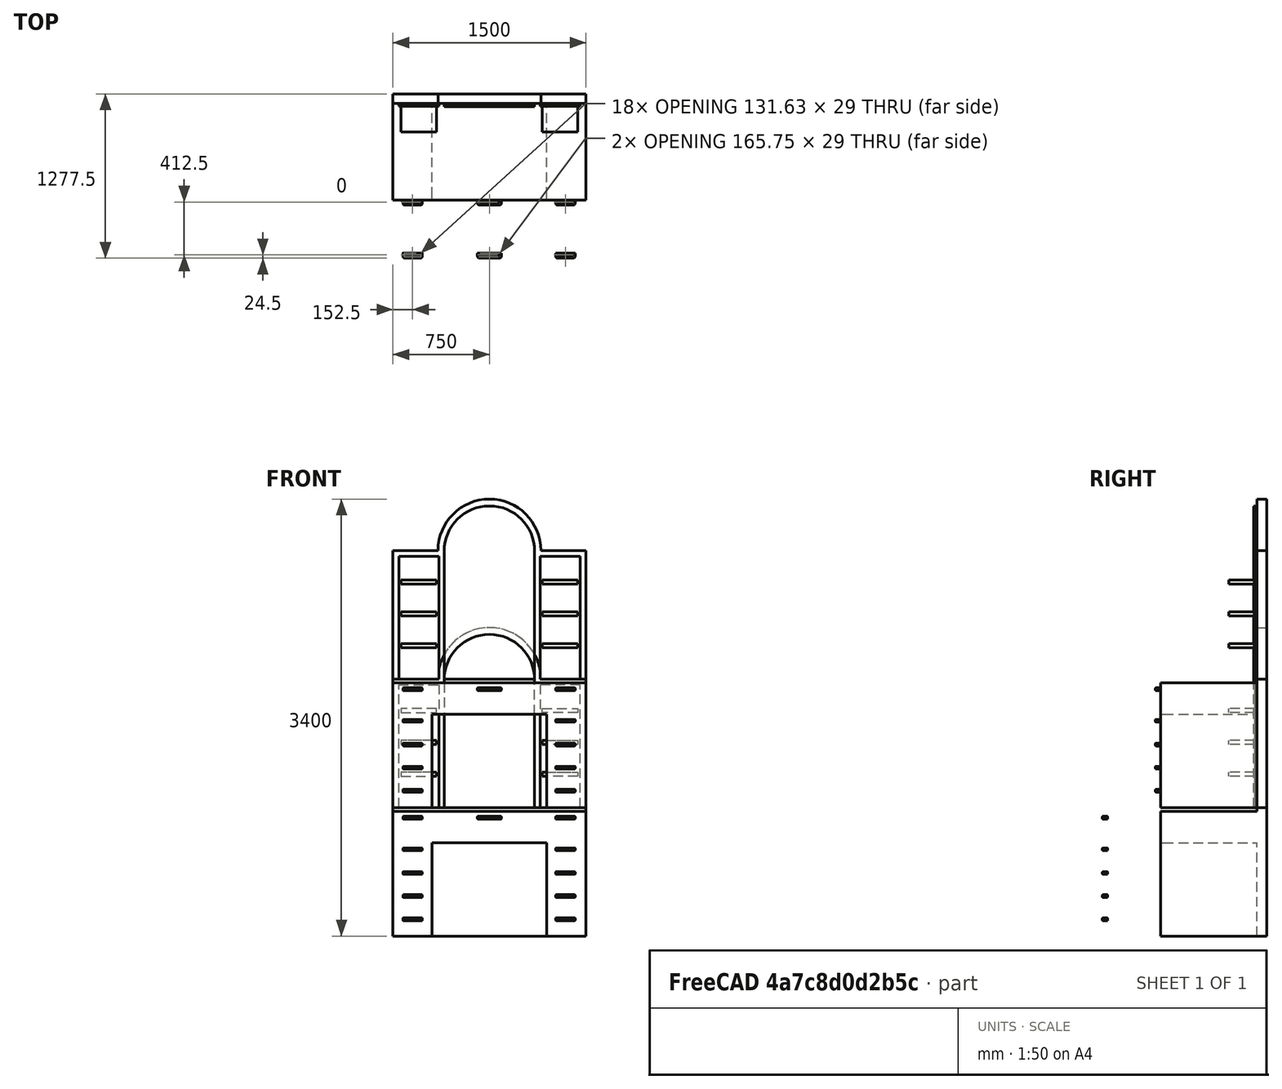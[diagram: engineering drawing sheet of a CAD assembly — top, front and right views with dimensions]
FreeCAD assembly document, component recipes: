
FREECAD ASSEMBLY — COMPONENT RECIPES ("DressingTable")

This assembly document has 3 components, labeled P0..P2 below (a component is one placed body or linked part). 3 of them carry a construction recipe — the FreeCAD feature program that regenerates the part from scratch, quoted from this document or its linked companion documents; the rest are supplied as boundary geometry only. No exploded tour is included for this assembly.
COMPONENT P0 — recipe-attached ("Body013", modeled in this document).
Construction recipe (the document's own serialized feature program — sketch geometry with constraints, then the solid features built on it; lengths are millimeters unless a unit is written):

FEATURE [PartDesign::ShapeBinder] CopyPad005
  Placement = pos=(0,-20,9e-15) rot=(0,0,1;0rad)
  TraceSupport = false
FEATURE [PartDesign::Plane] DatumPlane011
  AttachmentSupport = -> [CopyPad005]
  Length = 899.662
  MapMode = 5
  Placement = pos=(0,-95,2.55e-14) rot=(1,0,0;1.5708rad)
  ResizeMode = 0
  Width = 1568.05
FEATURE [Sketcher::SketchObject] Sketch030
  ArcFitTolerance = 1e-06
  AttachmentSupport = -> [CopyPad005]
  ExternalGeometry = -> [CopyPad005]
  FullyConstrained = false
  MakeInternals = false
  MapMode = 5
  Placement = pos=(0,-95,2.55e-14) rot=(1,0,0;1.5708rad)
  sketch-geometry (4):
    g0: LineSegment StartX=-351.618 StartY=995.137 StartZ=0 EndX=-351.618 EndY=0 EndZ=0
    g1: LineSegment StartX=-351.618 StartY=0 StartZ=0 EndX=351.618 EndY=0 EndZ=0
    g2: LineSegment StartX=351.618 StartY=0 StartZ=0 EndX=351.618 EndY=995.137 EndZ=0
    g3: ArcOfCircle CenterX=1.05374e-11 CenterY=995.137 CenterZ=0 NormalX=0 NormalY=0 NormalZ=1 AngleXU=0 Radius=351.618 StartAngle=8.98854e-10 EndAngle=3.14159
  constraints (10):
    c: Coincident(g0,g1)
    c: Coincident(g1,g2)
    c: Vertical(g0)
    c: Vertical(g2)
    c: Horizontal(g1)
    c: Coincident(g0,g-4)
    c: Coincident(g1,g-3)
    c: Coincident(g3,g0)
    c: Coincident(g3,g2)
    c: Tangent(g3,g-5)
FEATURE [PartDesign::Pad] Pad017
  Direction = (0,-1,2e-16)
  Length = 5
  Length2 = 10
  Placement = pos=(0,-20,9e-15) rot=(0,0,1;0rad)
  Profile = -> Sketch030
  ReferenceAxis = -> Sketch030 [N_Axis]
  Refine = true
  Suppressed = false
  Type = 0
FEATURE [PartDesign::Body] Body012
  AllowCompound = false
  Group = -> [DatumPlane011,CopyPad005,Sketch030,Pad017]
  Origin = -> Origin020
  Placement = pos=(0,412.5,0) rot=(0,0,1;0rad)
  Tip = -> Pad017
COMPONENT P1 — recipe-attached ("dressing_table002", modeled in this document).
Construction recipe (the document's own serialized feature program — sketch geometry with constraints, then the solid features built on it; lengths are millimeters unless a unit is written):

FEATURE [Sketcher::SketchObject] Sketch
  ArcFitTolerance = 1e-06
  AttachmentSupport = -> [XZ_Plane]
  FullyConstrained = true
  MakeInternals = false
  MapMode = 5
  Placement = pos=(0,0,0) rot=(1,0,0;1.5708rad)
  sketch-geometry (7):
    g0: LineSegment StartX=-750 StartY=-1000 StartZ=0 EndX=750 EndY=-1000 EndZ=0
    g1: LineSegment StartX=750 StartY=-1000 StartZ=0 EndX=750 EndY=1000 EndZ=0
    g2: LineSegment StartX=750 StartY=1000 StartZ=0 EndX=400 EndY=1000 EndZ=0
    g3: LineSegment StartX=-750 StartY=1000 StartZ=0 EndX=-750 EndY=-1000 EndZ=0
    g4: GeomPoint [constr] X=0 Y=0 Z=0
    g5: ArcOfCircle CenterX=1.35e-14 CenterY=1000 CenterZ=0 NormalX=0 NormalY=0 NormalZ=1 AngleXU=0 Radius=400 StartAngle=0 EndAngle=3.14159
    g6: LineSegment StartX=-400 StartY=1000 StartZ=0 EndX=-750 EndY=1000 EndZ=0
  constraints (18):
    c: Coincident(g0,g1)
    c: Coincident(g1,g2)
    c: Coincident(g6,g3)
    c: Coincident(g3,g0)
    c: Horizontal(g0)
    c: Horizontal(g2)
    c: Vertical(g1)
    c: Vertical(g3)
    c: Symmetric(g2,g0,g4)
    c: Coincident(g4,g-1)
    c: DistanceY(g1,g1) = 2000
    c: DistanceX(g6,g2) = 1500
    c: Symmetric(g1,g6,g5)
    c: Diameter(g5) = 800
    c: Coincident(g5,g6)
    c: Coincident(g5,g2)
    c: Horizontal(g6)
    c: Horizontal(g5,g2)
FEATURE [PartDesign::Pad] Pad
  Direction = (0,-1,2e-16)
  Length = 75
  Length2 = 10
  Placement = pos=(0,0,0) rot=(1,0,0;1.5708rad)
  Profile = -> Sketch
  ReferenceAxis = -> Sketch [N_Axis]
  Refine = true
  Suppressed = false
  Type = 0
FEATURE [Sketcher::SketchObject] Sketch001
  ArcFitTolerance = 1e-06
  AttachmentSupport = -> [Pad]
  FullyConstrained = false
  MakeInternals = false
  MapMode = 5
  Placement = pos=(0,-75,0) rot=(1,0,0;1.5708rad)
  sketch-geometry (14):
    g0: LineSegment [constr] StartX=0 StartY=0 StartZ=0 EndX=936.468 EndY=0 EndZ=0
    g1: LineSegment [constr] StartX=0 StartY=0 StartZ=0 EndX=-879.559 EndY=0 EndZ=0
    g2: ArcOfCircle CenterX=0 CenterY=995.137 CenterZ=0 NormalX=0 NormalY=0 NormalZ=1 AngleXU=0 Radius=351.618 StartAngle=0 EndAngle=3.14159
    g3: LineSegment StartX=-351.618 StartY=995.137 StartZ=0 EndX=-351.618 EndY=0 EndZ=0
    g4: LineSegment StartX=351.618 StartY=995.137 StartZ=0 EndX=351.618 EndY=0 EndZ=0
    g5: LineSegment StartX=-351.618 StartY=0 StartZ=0 EndX=351.618 EndY=0 EndZ=0
    g6: LineSegment StartX=393.332 StartY=955.725 StartZ=0 EndX=393.332 EndY=0 EndZ=0
    g7: LineSegment StartX=393.332 StartY=0 StartZ=0 EndX=704.851 EndY=0 EndZ=0
    g8: LineSegment StartX=704.851 StartY=0 StartZ=0 EndX=704.851 EndY=955.725 EndZ=0
    g9: LineSegment StartX=704.851 StartY=955.725 StartZ=0 EndX=393.332 EndY=955.725 EndZ=0
    g10: LineSegment StartX=-393.332 StartY=955.725 StartZ=0 EndX=-393.332 EndY=0 EndZ=0
    g11: LineSegment StartX=-393.332 StartY=0 StartZ=0 EndX=-704.851 EndY=0 EndZ=0
    g12: LineSegment StartX=-704.851 StartY=0 StartZ=0 EndX=-704.851 EndY=955.725 EndZ=0
    g13: LineSegment StartX=-704.851 StartY=955.725 StartZ=0 EndX=-393.332 EndY=955.725 EndZ=0
  constraints (30):
    c: Coincident(g0,g-1)
    c: Horizontal(g0)
    c: Coincident(g1,g0)
    c: PointOnObject(g1,g-1)
    c: PointOnObject(g2,g-2)
    c: PointOnObject(g3,g1)
    c: Vertical(g3)
    c: PointOnObject(g4,g0)
    c: Vertical(g4)
    c: Tangent(g4,g2) = 1.5708
    c: Tangent(g3,g2) = -1.5708
    c: Coincident(g5,g3)
    c: Coincident(g5,g4)
    c: Coincident(g6,g7)
    c: Coincident(g7,g8)
    c: Coincident(g8,g9)
    c: Coincident(g9,g6)
    c: Vertical(g6)
    c: Vertical(g8)
    c: Horizontal(g7)
    c: Horizontal(g9)
    c: PointOnObject(g7,g0)
    c: Coincident(g10,g11)
    c: Coincident(g11,g12)
    c: Coincident(g12,g13)
    c: Coincident(g13,g10)
    c: Vertical(g10)
    c: Vertical(g12)
    c: Horizontal(g11)
    c: Horizontal(g13)
FEATURE [PartDesign::Pad] Pad001
  BaseFeature = -> Pad
  Direction = (0,-1,2e-16)
  Length = 20
  Length2 = 10
  Placement = pos=(0,0,0) rot=(1,0,0;1.5708rad)
  Profile = -> Sketch001
  ReferenceAxis = -> Sketch001 [N_Axis]
  Refine = true
  Suppressed = false
  Type = 0
FEATURE [Sketcher::SketchObject] Sketch002
  ArcFitTolerance = 1e-06
  AttachmentSupport = -> [Pad001]
  ExternalGeometry = -> [Pad001]
  FullyConstrained = false
  MakeInternals = false
  MapMode = 5
  Placement = pos=(0,-95,2.09e-14) rot=(1,0,0;1.5708rad)
  sketch-geometry (27):
    g0: LineSegment StartX=-686.592 StartY=770.22 StartZ=0 EndX=-686.592 EndY=738.354 EndZ=0
    g1: LineSegment StartX=-686.592 StartY=738.354 StartZ=0 EndX=-411.592 EndY=738.354 EndZ=0
    g2: LineSegment StartX=-411.592 StartY=738.354 StartZ=0 EndX=-411.592 EndY=770.22 EndZ=0
    g3: LineSegment StartX=-411.592 StartY=770.22 StartZ=0 EndX=-686.592 EndY=770.22 EndZ=0
    g4: LineSegment StartX=-686.592 StartY=523.301 StartZ=0 EndX=-686.592 EndY=491.435 EndZ=0
    g5: LineSegment StartX=-686.592 StartY=491.435 StartZ=0 EndX=-411.592 EndY=491.435 EndZ=0
    g6: LineSegment StartX=-411.592 StartY=491.435 StartZ=0 EndX=-411.592 EndY=523.301 EndZ=0
    g7: LineSegment StartX=-411.592 StartY=523.301 StartZ=0 EndX=-686.592 EndY=523.301 EndZ=0
    g8: LineSegment StartX=-686.592 StartY=276.382 StartZ=0 EndX=-686.592 EndY=244.516 EndZ=0
    g9: LineSegment StartX=-686.592 StartY=244.516 StartZ=0 EndX=-411.592 EndY=244.516 EndZ=0
    g10: LineSegment StartX=-411.592 StartY=244.516 StartZ=0 EndX=-411.592 EndY=276.382 EndZ=0
    g11: LineSegment StartX=-411.592 StartY=276.382 StartZ=0 EndX=-686.592 EndY=276.382 EndZ=0
    g12: LineSegment [constr] StartX=-686.592 StartY=738.354 StartZ=0 EndX=-686.592 EndY=523.301 EndZ=0
    g13: LineSegment [constr] StartX=-686.592 StartY=491.435 StartZ=0 EndX=-686.592 EndY=276.382 EndZ=0
    g14: LineSegment [constr] StartX=-549.092 StartY=477.863 StartZ=0 EndX=-549.092 EndY=955.725 EndZ=0
    g15: LineSegment StartX=686.592 StartY=738.354 StartZ=0 EndX=411.592 EndY=738.354 EndZ=0
    g16: LineSegment StartX=411.592 StartY=770.22 StartZ=0 EndX=686.592 EndY=770.22 EndZ=0
    g17: LineSegment StartX=411.592 StartY=738.354 StartZ=0 EndX=411.592 EndY=770.22 EndZ=0
    g18: LineSegment StartX=686.592 StartY=770.22 StartZ=0 EndX=686.592 EndY=738.354 EndZ=0
    g19: LineSegment StartX=411.592 StartY=523.301 StartZ=0 EndX=686.592 EndY=523.301 EndZ=0
    g20: LineSegment StartX=411.592 StartY=491.435 StartZ=0 EndX=411.592 EndY=523.301 EndZ=0
    g21: LineSegment StartX=686.592 StartY=491.435 StartZ=0 EndX=411.592 EndY=491.435 EndZ=0
    g22: LineSegment StartX=686.592 StartY=523.301 StartZ=0 EndX=686.592 EndY=491.435 EndZ=0
    g23: LineSegment StartX=411.592 StartY=244.516 StartZ=0 EndX=411.592 EndY=276.382 EndZ=0
    g24: LineSegment StartX=686.592 StartY=244.516 StartZ=0 EndX=411.592 EndY=244.516 EndZ=0
    g25: LineSegment StartX=411.592 StartY=276.382 StartZ=0 EndX=686.592 EndY=276.382 EndZ=0
    g26: LineSegment StartX=686.592 StartY=276.382 StartZ=0 EndX=686.592 EndY=244.516 EndZ=0
  constraints (66):
    c: Coincident(g0,g1)
    c: Coincident(g1,g2)
    c: Coincident(g2,g3)
    c: Coincident(g3,g0)
    c: Vertical(g0)
    c: Vertical(g2)
    c: Horizontal(g1)
    c: Horizontal(g3)
    c: Coincident(g4,g5)
    c: Coincident(g5,g6)
    c: Coincident(g6,g7)
    c: Coincident(g7,g4)
    c: Vertical(g4)
    c: Vertical(g6)
    c: Horizontal(g5)
    c: Horizontal(g7)
    c: Coincident(g8,g9)
    c: Coincident(g9,g10)
    c: Coincident(g10,g11)
    c: Coincident(g11,g8)
    c: Vertical(g8)
    c: Vertical(g10)
    c: Horizontal(g9)
    c: Horizontal(g11)
    c: Coincident(g12,g0)
    c: Coincident(g12,g4)
    c: Vertical(g12)
    c: Coincident(g13,g4)
    c: Coincident(g13,g8)
    c: Vertical(g13)
    c: Equal(g12,g13)
    c: Equal(g2,g6)
    c: Equal(g6,g10)
    c: Equal(g11,g7)
    c: Equal(g7,g3)
    c: DistanceX(g3,g3) = 275
    c: Symmetric(g2,g0,g14)
    c: Symmetric(g-5,g-5,g14)
    c: Coincident(g18,g15)
    c: Coincident(g15,g17)
    c: Coincident(g17,g16)
    c: Coincident(g16,g18)
    c: Vertical(g18)
    c: Vertical(g17)
    c: Horizontal(g15)
    c: Horizontal(g16)
    c: Coincident(g22,g21)
    c: Coincident(g21,g20)
    c: Coincident(g20,g19)
    c: Coincident(g19,g22)
    c: Vertical(g22)
    c: Vertical(g20)
    c: Horizontal(g21)
    c: Horizontal(g19)
    c: Coincident(g26,g24)
    c: Coincident(g24,g23)
    c: Coincident(g23,g25)
    c: Coincident(g25,g26)
    c: Vertical(g26)
    c: Vertical(g23)
    c: Horizontal(g24)
    c: Horizontal(g25)
    c: Equal(g17,g20)
    c: Equal(g20,g23)
    c: Equal(g25,g19)
    c: Equal(g19,g16)
FEATURE [PartDesign::Pad] Pad002
  BaseFeature = -> Pad001
  Direction = (0,-1,2e-16)
  Length = 200
  Length2 = 10
  Placement = pos=(0,0,0) rot=(1,0,0;1.5708rad)
  Profile = -> Sketch002
  ReferenceAxis = -> Sketch002 [N_Axis]
  Refine = true
  Suppressed = false
  Type = 0
FEATURE [Sketcher::SketchObject] Sketch003
  ArcFitTolerance = 1e-06
  AttachmentSupport = -> [Pad002]
  ExternalGeometry = -> [Pad002]
  FullyConstrained = true
  MakeInternals = false
  MapMode = 5
  Placement = pos=(0,-75,0) rot=(1,0,0;1.5708rad)
  sketch-geometry (4):
    g0: LineSegment StartX=-750 StartY=-1000 StartZ=0 EndX=750 EndY=-1000 EndZ=0
    g1: LineSegment StartX=750 StartY=-1000 StartZ=0 EndX=750 EndY=-30 EndZ=0
    g2: LineSegment StartX=750 StartY=-30 StartZ=0 EndX=-750 EndY=-30 EndZ=0
    g3: LineSegment StartX=-750 StartY=-30 StartZ=0 EndX=-750 EndY=-1000 EndZ=0
  constraints (11):
    c: Coincident(g0,g1)
    c: Coincident(g1,g2)
    c: Coincident(g2,g3)
    c: Coincident(g3,g0)
    c: Horizontal(g0)
    c: Horizontal(g2)
    c: Vertical(g1)
    c: Vertical(g3)
    c: Coincident(g0,g-3)
    c: PointOnObject(g1,g-4)
    c: DistanceY(g1,g1) = 970
FEATURE [PartDesign::Pad] Pad003
  BaseFeature = -> Pad002
  Direction = (0,-1,2e-16)
  Length = 750
  Length2 = 10
  Placement = pos=(0,0,0) rot=(1,0,0;1.5708rad)
  Profile = -> Sketch003
  ReferenceAxis = -> Sketch003 [N_Axis]
  Suppressed = false
  Type = 0
FEATURE [Sketcher::SketchObject] Sketch004
  ArcFitTolerance = 1e-06
  AttachmentSupport = -> [Pad003]
  ExternalGeometry = -> [Pad003]
  FullyConstrained = true
  MakeInternals = false
  MapMode = 5
  Placement = pos=(0,-825,1.897e-13) rot=(1,0,0;1.5708rad)
  sketch-geometry (4):
    g0: LineSegment StartX=-445 StartY=-1000 StartZ=0 EndX=445 EndY=-1000 EndZ=0
    g1: LineSegment StartX=445 StartY=-1000 StartZ=0 EndX=445 EndY=-275 EndZ=0
    g2: LineSegment StartX=445 StartY=-275 StartZ=0 EndX=-445 EndY=-275 EndZ=0
    g3: LineSegment StartX=-445 StartY=-275 StartZ=0 EndX=-445 EndY=-1000 EndZ=0
  constraints (11):
    c: Coincident(g0,g1)
    c: Coincident(g1,g2)
    c: Coincident(g2,g3)
    c: Coincident(g3,g0)
    c: Horizontal(g0)
    c: Vertical(g1)
    c: Vertical(g3)
    c: PointOnObject(g0,g-3)
    c: DistanceX(g2,g2) = 890
    c: DistanceY(g1,g1) = 725
    c: Symmetric(g1,g2,g-2)
FEATURE [PartDesign::Pocket] Pocket
  BaseFeature = -> Pad003
  Direction = (0,1,-2e-16)
  Length = 750
  Length2 = 5
  Placement = pos=(0,0,0) rot=(1,0,0;1.5708rad)
  Profile = -> Sketch004
  ReferenceAxis = -> Sketch004 [N_Axis]
  Suppressed = false
  Type = 0
FEATURE [Sketcher::SketchObject] Sketch005
  ArcFitTolerance = 1e-06
  AttachmentSupport = -> [Pocket]
  ExternalGeometry = -> [Pocket]
  FullyConstrained = true
  MakeInternals = false
  MapMode = 5
  Placement = pos=(0,-825,1.897e-13) rot=(1,0,0;1.5708rad)
  sketch-geometry (24):
    g0: LineSegment StartX=-445 StartY=-275 StartZ=0 EndX=-445 EndY=-30 EndZ=0
    g1: LineSegment StartX=-445 StartY=-30 StartZ=0 EndX=-750 EndY=-30 EndZ=0
    g2: LineSegment StartX=-750 StartY=-30 StartZ=0 EndX=-750 EndY=-275 EndZ=0
    g3: LineSegment StartX=-750 StartY=-275 StartZ=0 EndX=-445 EndY=-275 EndZ=0
    g4: LineSegment StartX=-445 StartY=-460 StartZ=0 EndX=-750 EndY=-460 EndZ=0
    g5: LineSegment StartX=-750 StartY=-460 StartZ=0 EndX=-750 EndY=-640 EndZ=0
    g6: LineSegment StartX=-750 StartY=-640 StartZ=0 EndX=-445 EndY=-640 EndZ=0
    g7: LineSegment StartX=-445 StartY=-640 StartZ=0 EndX=-445 EndY=-460 EndZ=0
    g8: LineSegment StartX=-750 StartY=-820 StartZ=0 EndX=-445 EndY=-820 EndZ=0
    g9: LineSegment StartX=-750 StartY=-820 StartZ=0 EndX=-750 EndY=-1000 EndZ=0
    g10: LineSegment StartX=-750 StartY=-1000 StartZ=0 EndX=-445 EndY=-1000 EndZ=0
    g11: LineSegment StartX=-445 StartY=-1000 StartZ=0 EndX=-445 EndY=-820 EndZ=0
    g12: LineSegment StartX=750 StartY=-30 StartZ=0 EndX=750 EndY=-275 EndZ=0
    g13: LineSegment StartX=445 StartY=-30 StartZ=0 EndX=750 EndY=-30 EndZ=0
    g14: LineSegment StartX=750 StartY=-275 StartZ=0 EndX=445 EndY=-275 EndZ=0
    g15: LineSegment StartX=445 StartY=-460 StartZ=0 EndX=750 EndY=-460 EndZ=0
    g16: LineSegment StartX=750 StartY=-460 StartZ=0 EndX=750 EndY=-640 EndZ=0
    g17: LineSegment StartX=750 StartY=-640 StartZ=0 EndX=445 EndY=-640 EndZ=0
    g18: LineSegment StartX=445 StartY=-640 StartZ=0 EndX=445 EndY=-460 EndZ=0
    g19: LineSegment StartX=445 StartY=-1000 StartZ=0 EndX=445 EndY=-820 EndZ=0
    g20: LineSegment StartX=750 StartY=-1000 StartZ=0 EndX=445 EndY=-1000 EndZ=0
    g21: LineSegment StartX=750 StartY=-820 StartZ=0 EndX=750 EndY=-1000 EndZ=0
    g22: LineSegment StartX=750 StartY=-820 StartZ=0 EndX=445 EndY=-820 EndZ=0
    g23: LineSegment StartX=445 StartY=-30 StartZ=0 EndX=445 EndY=-275 EndZ=0
  constraints (67):
    c: Coincident(g0,g1)
    c: Vertical(g0)
    c: Horizontal(g1)
    c: Coincident(g0,g-6)
    c: Coincident(g1,g2)
    c: PointOnObject(g2,g-5)
    c: Coincident(g2,g3)
    c: Coincident(g3,g0)
    c: Horizontal(g3)
    c: PointOnObject(g4,g-6)
    c: PointOnObject(g4,g-5)
    c: Horizontal(g4)
    c: Coincident(g4,g5)
    c: PointOnObject(g5,g-5)
    c: Coincident(g5,g6)
    c: PointOnObject(g6,g-6)
    c: Horizontal(g6)
    c: Coincident(g6,g7)
    c: PointOnObject(g8,g-5)
    c: PointOnObject(g8,g-6)
    c: Horizontal(g8)
    c: Coincident(g9,g10)
    c: PointOnObject(g10,g-6)
    c: Horizontal(g10)
    c: Coincident(g10,g11)
    c: Coincident(g11,g8)
    c: Coincident(g9,g-5)
    c: DistanceY(g9,g9) = 180
    c: Coincident(g1,g-5)
    c: Horizontal(g13)
    c: Coincident(g13,g12)
    c: Coincident(g12,g14)
    c: Horizontal(g14)
    c: Horizontal(g15)
    c: Coincident(g15,g16)
    c: Coincident(g16,g17)
    c: Horizontal(g17)
    c: Coincident(g17,g18)
    c: Horizontal(g22)
    c: Coincident(g21,g20)
    c: Horizontal(g20)
    c: Coincident(g20,g19)
    c: Coincident(g19,g22)
    c: Coincident(g12,g-4)
    c: Equal(g14,g13)
    c: Horizontal(g15,g4)
    c: Horizontal(g17,g6)
    c: Horizontal(g22,g8)
    c: Horizontal(g19,g10)
    c: Vertical(g15,g17)
    c: Vertical(g17,g22)
    c: Vertical(g22,g19)
    c: Vertical(g19,g14)
    c: Vertical(g21,g20)
    c: Vertical(g20,g12)
    c: Coincident(g23,g13)
    c: Coincident(g23,g14)
    c: Vertical(g23)
    c: Coincident(g14,g-3)
    c: Coincident(g7,g4)
    c: Equal(g5,g9)
    c: Coincident(g18,g15)
    c: Vertical(g15,g12)
    c: Coincident(g22,g21)
    c: Coincident(g9,g8)
    c: DistanceY(g8,g5) = 180
    c: Vertical(g16,g21)
FEATURE [PartDesign::Pad] Pad004
  BaseFeature = -> Pocket
  Direction = (0,-1,2e-16)
  Length = 25
  Length2 = 10
  Placement = pos=(0,0,0) rot=(1,0,0;1.5708rad)
  Profile = -> Sketch005
  ReferenceAxis = -> Sketch005 [N_Axis]
  Reversed = true
  Suppressed = false
  Type = 0
FEATURE [Sketcher::SketchObject] Sketch006
  ArcFitTolerance = 1e-06
  AttachmentSupport = -> [Pad004]
  ExternalGeometry = -> [Pad004]
  FullyConstrained = true
  MakeInternals = false
  MapMode = 5
  Placement = pos=(0,-825,1.897e-13) rot=(1,0,0;1.5708rad)
  sketch-geometry (20):
    g0: LineSegment StartX=-750 StartY=-275 StartZ=0 EndX=-750 EndY=-460 EndZ=0
    g1: LineSegment StartX=-750 StartY=-460 StartZ=0 EndX=-445 EndY=-460 EndZ=0
    g2: LineSegment StartX=-445 StartY=-460 StartZ=0 EndX=-445 EndY=-275 EndZ=0
    g3: LineSegment StartX=-445 StartY=-275 StartZ=0 EndX=-750 EndY=-275 EndZ=0
    g4: LineSegment StartX=-750 StartY=-640 StartZ=0 EndX=-750 EndY=-820 EndZ=0
    g5: LineSegment StartX=-750 StartY=-820 StartZ=0 EndX=-445 EndY=-820 EndZ=0
    g6: LineSegment StartX=-445 StartY=-820 StartZ=0 EndX=-445 EndY=-640 EndZ=0
    g7: LineSegment StartX=-445 StartY=-640 StartZ=0 EndX=-750 EndY=-640 EndZ=0
    g8: LineSegment StartX=445 StartY=-275 StartZ=0 EndX=445 EndY=-460 EndZ=0
    g9: LineSegment StartX=445 StartY=-460 StartZ=0 EndX=750 EndY=-460 EndZ=0
    g10: LineSegment StartX=750 StartY=-460 StartZ=0 EndX=750 EndY=-275 EndZ=0
    g11: LineSegment StartX=750 StartY=-275 StartZ=0 EndX=445 EndY=-275 EndZ=0
    g12: LineSegment StartX=445 StartY=-640 StartZ=0 EndX=445 EndY=-820 EndZ=0
    g13: LineSegment StartX=445 StartY=-820 StartZ=0 EndX=750 EndY=-820 EndZ=0
    g14: LineSegment StartX=750 StartY=-820 StartZ=0 EndX=750 EndY=-640 EndZ=0
    g15: LineSegment StartX=750 StartY=-640 StartZ=0 EndX=445 EndY=-640 EndZ=0
    g16: LineSegment StartX=-445 StartY=-30 StartZ=0 EndX=-445 EndY=-275 EndZ=0
    g17: LineSegment StartX=-445 StartY=-275 StartZ=0 EndX=445 EndY=-275 EndZ=0
    g18: LineSegment StartX=445 StartY=-275 StartZ=0 EndX=445 EndY=-30 EndZ=0
    g19: LineSegment StartX=445 StartY=-30 StartZ=0 EndX=-445 EndY=-30 EndZ=0
  constraints (50):
    c: Coincident(g0,g1)
    c: Coincident(g1,g2)
    c: Coincident(g2,g3)
    c: Coincident(g3,g0)
    c: Vertical(g0)
    c: Vertical(g2)
    c: Horizontal(g1)
    c: Horizontal(g3)
    c: Coincident(g0,g-4)
    c: Coincident(g1,g-3)
    c: Coincident(g4,g5)
    c: Coincident(g5,g6)
    c: Coincident(g6,g7)
    c: Coincident(g7,g4)
    c: Vertical(g4)
    c: Vertical(g6)
    c: Horizontal(g5)
    c: Horizontal(g7)
    c: Coincident(g4,g-6)
    c: Coincident(g5,g-5)
    c: Coincident(g8,g9)
    c: Coincident(g9,g10)
    c: Coincident(g10,g11)
    c: Coincident(g11,g8)
    c: Vertical(g8)
    c: Vertical(g10)
    c: Horizontal(g9)
    c: Horizontal(g11)
    c: Coincident(g8,g-8)
    c: Coincident(g9,g-9)
    c: Coincident(g12,g13)
    c: Coincident(g13,g14)
    c: Coincident(g14,g15)
    c: Coincident(g15,g12)
    c: Vertical(g12)
    c: Vertical(g14)
    c: Horizontal(g13)
    c: Horizontal(g15)
    c: Coincident(g12,g-10)
    c: Coincident(g13,g-11)
    c: Coincident(g16,g17)
    c: Coincident(g17,g18)
    c: Coincident(g18,g19)
    c: Coincident(g19,g16)
    c: Vertical(g16)
    c: Vertical(g18)
    c: Horizontal(g17)
    c: Horizontal(g19)
    c: Coincident(g16,g-7)
    c: Coincident(g17,g8)
FEATURE [PartDesign::Pad] Pad005
  BaseFeature = -> Pad004
  Direction = (0,-1,2e-16)
  Length = 25
  Length2 = 10
  Placement = pos=(0,0,0) rot=(1,0,0;1.5708rad)
  Profile = -> Sketch006
  ReferenceAxis = -> Sketch006 [N_Axis]
  Reversed = true
  Suppressed = false
  Type = 0
FEATURE [PartDesign::Body] Body
  AllowCompound = false
  Group = -> [Sketch,Pad,Sketch001,Pad001,Sketch002,Pad002,Sketch003,Pad003,Sketch004,Pocket,Sketch005,Pad004,Sketch006,Pad005]
  Origin = -> Origin
  Placement = pos=(0,412.5,0) rot=(0,0,1;0rad)
  Tip = -> Pad005
COMPONENT P2 — recipe-attached ("handle_p001", modeled in this document).
Construction recipe (the document's own serialized feature program — sketch geometry with constraints, then the solid features built on it; lengths are millimeters unless a unit is written):

FEATURE [PartDesign::ShapeBinder] CopyPocket001
  Placement = pos=(0,0,0) rot=(1,0,0;1.5708rad)
  TraceSupport = false
FEATURE [PartDesign::Plane] DatumPlane
  AttachmentSupport = -> [CopyPocket001]
  Length = 214.996
  MapMode = 5
  Placement = pos=(0,-825,3.729e-13) rot=(1,0,0;1.5708rad)
  ResizeMode = 0
  Width = 144.392
FEATURE [Sketcher::SketchObject] Sketch008
  ArcFitTolerance = 1e-06
  AttachmentSupport = -> [CopyPocket001]
  ExternalGeometry = -> [CopyPocket001]
  FullyConstrained = true
  MakeInternals = false
  MapMode = 5
  Placement = pos=(0,-825,3.729e-13) rot=(1,0,0;1.5708rad)
  sketch-geometry (4):
    g0: LineSegment StartX=-92.8734 StartY=-68.8715 StartZ=0 EndX=-92.8734 EndY=-90.1429 EndZ=0
    g1: LineSegment StartX=-92.8734 StartY=-90.1429 StartZ=0 EndX=92.8734 EndY=-90.1429 EndZ=0
    g2: LineSegment StartX=92.8734 StartY=-90.1429 StartZ=0 EndX=92.8734 EndY=-68.8715 EndZ=0
    g3: LineSegment StartX=92.8734 StartY=-68.8715 StartZ=0 EndX=-92.8734 EndY=-68.8715 EndZ=0
  constraints (10):
    c: Coincident(g0,g1)
    c: Coincident(g1,g2)
    c: Coincident(g2,g3)
    c: Coincident(g3,g0)
    c: Vertical(g0)
    c: Vertical(g2)
    c: Horizontal(g1)
    c: Horizontal(g3)
    c: Coincident(g0,g-3)
    c: Coincident(g1,g-5)
FEATURE [PartDesign::Pad] Pad006
  Direction = (0,-1,2e-16)
  Length = 40
  Length2 = 10
  Placement = pos=(0,0,0) rot=(1,0,0;1.5708rad)
  Profile = -> Sketch008
  ReferenceAxis = -> Sketch008 [N_Axis]
  Refine = true
  Suppressed = false
  Type = 0
FEATURE [Sketcher::SketchObject] Sketch009
  ArcFitTolerance = 1e-06
  AttachmentSupport = -> [Pad006]
  ExternalGeometry = -> [Pad006]
  FullyConstrained = true
  MakeInternals = false
  MapMode = 5
  Placement = pos=(0,-2.29e-14,-68.8715) rot=(0,0,1;3.14159rad)
  sketch-geometry (4):
    g0: LineSegment StartX=-77.8734 StartY=850 StartZ=0 EndX=-77.8734 EndY=826 EndZ=0
    g1: LineSegment StartX=77.8734 StartY=850 StartZ=0 EndX=77.8734 EndY=826 EndZ=0
    g2: LineSegment StartX=-77.8734 StartY=850 StartZ=0 EndX=77.8734 EndY=850 EndZ=0
    g3: LineSegment StartX=-77.8734 StartY=826 StartZ=0 EndX=77.8734 EndY=826 EndZ=0
  constraints (12):
    c: Coincident(g2,g0)
    c: Coincident(g2,g1)
    c: Horizontal(g2)
    c: DistanceX(g-3,g0) = 15
    c: DistanceX(g1,g-3) = 15
    c: Vertical(g0)
    c: Vertical(g1)
    c: DistanceY(g0,g-4) = 15
    c: DistanceY(g-3,g0) = 1
    c: DistanceY(g-3,g1) = 1
    c: Coincident(g3,g0)
    c: Coincident(g3,g1)
FEATURE [PartDesign::Pocket] Pocket002
  BaseFeature = -> Pad006
  Direction = (0,0,-1)
  Length = 5
  Length2 = 5
  Placement = pos=(0,0,0) rot=(1,0,0;1.5708rad)
  Profile = -> Sketch009
  ReferenceAxis = -> Sketch009 [N_Axis]
  Refine = true
  Suppressed = false
  Type = 1
FEATURE [PartDesign::Fillet] Fillet
  Base = -> Pocket002 [Edge22,Edge21,Edge4,Edge20]
  BaseFeature = -> Pocket002
  Placement = pos=(0,0,0) rot=(1,0,0;1.5708rad)
  Radius = 15
  Refine = true
  SupportTransform = false
  Suppressed = false
  UseAllEdges = false
FEATURE [PartDesign::Fillet] Fillet001
  Base = -> Fillet [Edge8,Edge20,Edge10,Edge26]
  BaseFeature = -> Fillet
  Placement = pos=(0,0,0) rot=(1,0,0;1.5708rad)
  Radius = 5
  Refine = true
  SupportTransform = false
  Suppressed = false
  UseAllEdges = false
FEATURE [PartDesign::Body] Body001
  AllowCompound = false
  Group = -> [DatumPlane,CopyPocket001,Sketch008,Pad006,Sketch009,Pocket002,Fillet,Fillet001]
  Origin = -> Origin005
  Tip = -> Fillet001
FEATURE [PartDesign::ShapeBinder] CopyPocket002
  Placement = pos=(0,0,0) rot=(1,0,0;1.5708rad)
  TraceSupport = false
FEATURE [PartDesign::Plane] DatumPlane001
  AttachmentSupport = -> [CopyPocket002]
  Length = 755.028
  MapMode = 5
  Placement = pos=(0,-825,3.729e-13) rot=(1,0,0;1.5708rad)
  ResizeMode = 0
  Width = 171.855
FEATURE [Sketcher::SketchObject] Sketch010
  ArcFitTolerance = 1e-06
  AttachmentSupport = -> [CopyPocket002]
  ExternalGeometry = -> [CopyPocket002]
  FullyConstrained = true
  MakeInternals = false
  MapMode = 5
  Placement = pos=(0,-825,3.729e-13) rot=(1,0,0;1.5708rad)
  sketch-geometry (4):
    g0: LineSegment StartX=-673.316 StartY=-90.1429 StartZ=0 EndX=-521.684 EndY=-90.1429 EndZ=0
    g1: LineSegment StartX=-521.684 StartY=-90.1429 StartZ=0 EndX=-521.684 EndY=-68.8715 EndZ=0
    g2: LineSegment StartX=-521.684 StartY=-68.8715 StartZ=0 EndX=-673.316 EndY=-68.8715 EndZ=0
    g3: LineSegment StartX=-673.316 StartY=-68.8715 StartZ=0 EndX=-673.316 EndY=-90.1429 EndZ=0
  constraints (10):
    c: Coincident(g0,g1)
    c: Coincident(g1,g2)
    c: Coincident(g2,g3)
    c: Coincident(g3,g0)
    c: Horizontal(g0)
    c: Horizontal(g2)
    c: Vertical(g1)
    c: Vertical(g3)
    c: Coincident(g0,g-4)
    c: Coincident(g1,g-3)
FEATURE [PartDesign::Pad] Pad007
  Direction = (0,-1,2e-16)
  Length = 40
  Length2 = 10
  Placement = pos=(0,0,0) rot=(1,0,0;1.5708rad)
  Profile = -> Sketch010
  ReferenceAxis = -> Sketch010 [N_Axis]
  Refine = true
  Suppressed = false
  Type = 0
FEATURE [Sketcher::SketchObject] Sketch011
  ArcFitTolerance = 1e-06
  AttachmentSupport = -> [Pad007]
  ExternalGeometry = -> [Pad007]
  FullyConstrained = true
  MakeInternals = false
  MapMode = 5
  Placement = pos=(0,-2.29e-14,-68.8715) rot=(0,0,1;3.14159rad)
  sketch-geometry (4):
    g0: LineSegment StartX=536.684 StartY=850 StartZ=0 EndX=536.684 EndY=826 EndZ=0
    g1: LineSegment StartX=536.684 StartY=826 StartZ=0 EndX=658.316 EndY=826 EndZ=0
    g2: LineSegment StartX=658.316 StartY=826 StartZ=0 EndX=658.316 EndY=850 EndZ=0
    g3: LineSegment StartX=658.316 StartY=850 StartZ=0 EndX=536.684 EndY=850 EndZ=0
  constraints (12):
    c: Coincident(g0,g1)
    c: Coincident(g1,g2)
    c: Coincident(g2,g3)
    c: Coincident(g3,g0)
    c: Vertical(g0)
    c: Vertical(g2)
    c: Horizontal(g1)
    c: Horizontal(g3)
    c: DistanceY(g-4,g1) = 1
    c: DistanceX(g1,g-4) = 15
    c: DistanceY(g2,g-4) = 15
    c: DistanceX(g-3,g0) = 15
FEATURE [PartDesign::Pocket] Pocket003
  BaseFeature = -> Pad007
  Direction = (0,0,-1)
  Length = 5
  Length2 = 5
  Placement = pos=(0,0,0) rot=(1,0,0;1.5708rad)
  Profile = -> Sketch011
  ReferenceAxis = -> Sketch011 [N_Axis]
  Refine = true
  Suppressed = false
  Type = 1
FEATURE [PartDesign::Fillet] Fillet002
  Base = -> Pocket003 [Edge19,Edge14,Edge23,Edge11]
  BaseFeature = -> Pocket003
  Placement = pos=(0,0,0) rot=(1,0,0;1.5708rad)
  Radius = 15
  Refine = true
  SupportTransform = false
  Suppressed = false
  UseAllEdges = false
FEATURE [PartDesign::Fillet] Fillet003
  Base = -> Fillet002 [Edge21,Edge4,Edge32,Edge10]
  BaseFeature = -> Fillet002
  Placement = pos=(0,0,0) rot=(1,0,0;1.5708rad)
  Radius = 5
  Refine = true
  SupportTransform = false
  Suppressed = false
  UseAllEdges = false
FEATURE [PartDesign::Body] Body002
  AllowCompound = false
  Group = -> [DatumPlane001,CopyPocket002,Sketch010,Pad007,Sketch011,Pocket003,Fillet002,Fillet003]
  Origin = -> Origin007
  Tip = -> Fillet003
FEATURE [PartDesign::ShapeBinder] CopyPocket003
  Placement = pos=(0,0,0) rot=(1,0,0;1.5708rad)
  TraceSupport = false
FEATURE [PartDesign::Plane] DatumPlane002
  AttachmentSupport = -> [CopyPocket003]
  Length = 798.615
  MapMode = 5
  Placement = pos=(0,-825,3.729e-13) rot=(1,0,0;1.5708rad)
  ResizeMode = 0
  Width = 460.441
FEATURE [Sketcher::SketchObject] Sketch012
  ArcFitTolerance = 1e-06
  AttachmentSupport = -> [CopyPocket003]
  ExternalGeometry = -> [CopyPocket003]
  FullyConstrained = true
  MakeInternals = false
  MapMode = 5
  Placement = pos=(0,-825,3.729e-13) rot=(1,0,0;1.5708rad)
  sketch-geometry (4):
    g0: LineSegment StartX=-673.316 StartY=-313.872 StartZ=0 EndX=-673.316 EndY=-335.143 EndZ=0
    g1: LineSegment StartX=-673.316 StartY=-335.143 StartZ=0 EndX=-521.684 EndY=-335.143 EndZ=0
    g2: LineSegment StartX=-521.684 StartY=-335.143 StartZ=0 EndX=-521.684 EndY=-313.872 EndZ=0
    g3: LineSegment StartX=-521.684 StartY=-313.872 StartZ=0 EndX=-673.316 EndY=-313.872 EndZ=0
  constraints (10):
    c: Coincident(g0,g1)
    c: Coincident(g1,g2)
    c: Coincident(g2,g3)
    c: Coincident(g3,g0)
    c: Vertical(g0)
    c: Vertical(g2)
    c: Horizontal(g1)
    c: Horizontal(g3)
    c: Coincident(g0,g-4)
    c: Coincident(g1,g-3)
FEATURE [PartDesign::Pad] Pad008
  Direction = (0,-1,2e-16)
  Length = 40
  Length2 = 10
  Placement = pos=(0,0,0) rot=(1,0,0;1.5708rad)
  Profile = -> Sketch012
  ReferenceAxis = -> Sketch012 [N_Axis]
  Refine = true
  Suppressed = false
  Type = 0
FEATURE [Sketcher::SketchObject] Sketch013
  ArcFitTolerance = 1e-06
  AttachmentSupport = -> [Pad008]
  ExternalGeometry = -> [Pad008]
  FullyConstrained = true
  MakeInternals = false
  MapMode = 5
  Placement = pos=(0,-1.045e-13,-313.872) rot=(0,0,1;3.14159rad)
  sketch-geometry (4):
    g0: LineSegment StartX=536.684 StartY=850 StartZ=0 EndX=536.684 EndY=826 EndZ=0
    g1: LineSegment StartX=536.684 StartY=826 StartZ=0 EndX=658.316 EndY=826 EndZ=0
    g2: LineSegment StartX=658.316 StartY=826 StartZ=0 EndX=658.316 EndY=850 EndZ=0
    g3: LineSegment StartX=658.316 StartY=850 StartZ=0 EndX=536.684 EndY=850 EndZ=0
  constraints (12):
    c: Coincident(g0,g1)
    c: Coincident(g1,g2)
    c: Coincident(g2,g3)
    c: Coincident(g3,g0)
    c: Vertical(g0)
    c: Vertical(g2)
    c: Horizontal(g1)
    c: Horizontal(g3)
    c: DistanceY(g-4,g1) = 1
    c: DistanceX(g1,g-4) = 15
    c: DistanceY(g0,g-3) = 15
    c: DistanceX(g-3,g0) = 15
FEATURE [PartDesign::Pocket] Pocket004
  BaseFeature = -> Pad008
  Direction = (0,0,-1)
  Length = 5
  Length2 = 5
  Placement = pos=(0,0,0) rot=(1,0,0;1.5708rad)
  Profile = -> Sketch013
  ReferenceAxis = -> Sketch013 [N_Axis]
  Refine = true
  Suppressed = false
  Type = 1
FEATURE [PartDesign::Fillet] Fillet004
  Base = -> Pocket004 [Edge20,Edge4,Edge21,Edge22]
  BaseFeature = -> Pocket004
  Placement = pos=(0,0,0) rot=(1,0,0;1.5708rad)
  Radius = 15
  Refine = true
  SupportTransform = false
  Suppressed = false
  UseAllEdges = false
FEATURE [PartDesign::Fillet] Fillet005
  Base = -> Fillet004 [Edge8,Edge20,Edge10,Edge26]
  BaseFeature = -> Fillet004
  Placement = pos=(0,0,0) rot=(1,0,0;1.5708rad)
  Radius = 5
  Refine = true
  SupportTransform = false
  Suppressed = false
  UseAllEdges = false
FEATURE [PartDesign::Body] Body003
  AllowCompound = false
  Group = -> [DatumPlane002,CopyPocket003,Sketch012,Pad008,Sketch013,Pocket004,Fillet004,Fillet005]
  Origin = -> Origin008
  Tip = -> Fillet005
FEATURE [PartDesign::ShapeBinder] CopyPocket004
  Placement = pos=(0,0,0) rot=(1,0,0;1.5708rad)
  TraceSupport = false
FEATURE [PartDesign::Plane] DatumPlane003
  AttachmentSupport = -> [CopyPocket004]
  Length = 821.715
  MapMode = 5
  Placement = pos=(0,-825,3.729e-13) rot=(1,0,0;1.5708rad)
  ResizeMode = 0
  Width = 668.542
FEATURE [Sketcher::SketchObject] Sketch014
  ArcFitTolerance = 1e-06
  AttachmentSupport = -> [CopyPocket004]
  ExternalGeometry = -> [CopyPocket004]
  FullyConstrained = true
  MakeInternals = false
  MapMode = 5
  Placement = pos=(0,-825,3.729e-13) rot=(1,0,0;1.5708rad)
  sketch-geometry (4):
    g0: LineSegment StartX=-673.316 StartY=-498.872 StartZ=0 EndX=-673.316 EndY=-520.143 EndZ=0
    g1: LineSegment StartX=-673.316 StartY=-520.143 StartZ=0 EndX=-521.684 EndY=-520.143 EndZ=0
    g2: LineSegment StartX=-521.684 StartY=-520.143 StartZ=0 EndX=-521.684 EndY=-498.872 EndZ=0
    g3: LineSegment StartX=-521.684 StartY=-498.872 StartZ=0 EndX=-673.316 EndY=-498.872 EndZ=0
  constraints (10):
    c: Coincident(g0,g1)
    c: Coincident(g1,g2)
    c: Coincident(g2,g3)
    c: Coincident(g3,g0)
    c: Vertical(g0)
    c: Vertical(g2)
    c: Horizontal(g1)
    c: Horizontal(g3)
    c: Coincident(g0,g-3)
    c: Coincident(g1,g-4)
FEATURE [PartDesign::Pad] Pad009
  Direction = (0,-1,2e-16)
  Length = 40
  Length2 = 10
  Placement = pos=(0,0,0) rot=(1,0,0;1.5708rad)
  Profile = -> Sketch014
  ReferenceAxis = -> Sketch014 [N_Axis]
  Refine = true
  Suppressed = false
  Type = 0
FEATURE [Sketcher::SketchObject] Sketch015
  ArcFitTolerance = 1e-06
  AttachmentSupport = -> [Pad009]
  ExternalGeometry = -> [Pad009]
  FullyConstrained = true
  MakeInternals = false
  MapMode = 5
  Placement = pos=(0,-1.662e-13,-498.872) rot=(0,0,1;3.14159rad)
  sketch-geometry (4):
    g0: LineSegment StartX=536.684 StartY=850 StartZ=0 EndX=536.684 EndY=826 EndZ=0
    g1: LineSegment StartX=536.684 StartY=826 StartZ=0 EndX=658.316 EndY=826 EndZ=0
    g2: LineSegment StartX=658.316 StartY=826 StartZ=0 EndX=658.316 EndY=850 EndZ=0
    g3: LineSegment StartX=658.316 StartY=850 StartZ=0 EndX=536.684 EndY=850 EndZ=0
  constraints (12):
    c: Coincident(g0,g1)
    c: Coincident(g1,g2)
    c: Coincident(g2,g3)
    c: Coincident(g3,g0)
    c: Vertical(g0)
    c: Vertical(g2)
    c: Horizontal(g1)
    c: Horizontal(g3)
    c: DistanceX(g1,g-4) = 15
    c: DistanceY(g-4,g1) = 1
    c: DistanceY(g0,g-3) = 15
    c: DistanceX(g-3,g0) = 15
FEATURE [PartDesign::Pocket] Pocket005
  BaseFeature = -> Pad009
  Direction = (0,0,-1)
  Length = 5
  Length2 = 5
  Placement = pos=(0,0,0) rot=(1,0,0;1.5708rad)
  Profile = -> Sketch015
  ReferenceAxis = -> Sketch015 [N_Axis]
  Refine = true
  Suppressed = false
  Type = 1
FEATURE [PartDesign::Fillet] Fillet006
  Base = -> Pocket005 [Edge22,Edge21,Edge4,Edge20]
  BaseFeature = -> Pocket005
  Placement = pos=(0,0,0) rot=(1,0,0;1.5708rad)
  Radius = 15
  Refine = true
  SupportTransform = false
  Suppressed = false
  UseAllEdges = false
FEATURE [PartDesign::Fillet] Fillet007
  Base = -> Fillet006 [Edge10,Edge1,Edge20,Edge4]
  BaseFeature = -> Fillet006
  Placement = pos=(0,0,0) rot=(1,0,0;1.5708rad)
  Radius = 5
  Refine = true
  SupportTransform = false
  Suppressed = false
  UseAllEdges = false
FEATURE [PartDesign::Body] Body004
  AllowCompound = false
  Group = -> [DatumPlane003,CopyPocket004,Sketch014,Pad009,Sketch015,Pocket005,Fillet006,Fillet007]
  Origin = -> Origin009
  Tip = -> Fillet007
FEATURE [PartDesign::ShapeBinder] CopyPocket005
  Placement = pos=(0,0,0) rot=(1,0,0;1.5708rad)
  TraceSupport = false
FEATURE [PartDesign::Plane] DatumPlane004
  AttachmentSupport = -> [CopyPocket005]
  Length = 840.637
  MapMode = 5
  Placement = pos=(0,-825,3.729e-13) rot=(1,0,0;1.5708rad)
  ResizeMode = 0
  Width = 867.464
FEATURE [Sketcher::SketchObject] Sketch016
  ArcFitTolerance = 1e-06
  AttachmentSupport = -> [CopyPocket005]
  ExternalGeometry = -> [CopyPocket005]
  FullyConstrained = true
  MakeInternals = false
  MapMode = 5
  Placement = pos=(0,-825,3.729e-13) rot=(1,0,0;1.5708rad)
  sketch-geometry (4):
    g0: LineSegment StartX=-673.316 StartY=-678.872 StartZ=0 EndX=-673.316 EndY=-700.143 EndZ=0
    g1: LineSegment StartX=-673.316 StartY=-700.143 StartZ=0 EndX=-521.684 EndY=-700.143 EndZ=0
    g2: LineSegment StartX=-521.684 StartY=-700.143 StartZ=0 EndX=-521.684 EndY=-678.872 EndZ=0
    g3: LineSegment StartX=-521.684 StartY=-678.872 StartZ=0 EndX=-673.316 EndY=-678.872 EndZ=0
  constraints (10):
    c: Coincident(g0,g1)
    c: Coincident(g1,g2)
    c: Coincident(g2,g3)
    c: Coincident(g3,g0)
    c: Vertical(g0)
    c: Vertical(g2)
    c: Horizontal(g1)
    c: Horizontal(g3)
    c: Coincident(g0,g-4)
    c: Coincident(g1,g-3)
FEATURE [PartDesign::Pad] Pad010
  Direction = (0,-1,2e-16)
  Length = 40
  Length2 = 10
  Placement = pos=(0,0,0) rot=(1,0,0;1.5708rad)
  Profile = -> Sketch016
  ReferenceAxis = -> Sketch016 [N_Axis]
  Refine = true
  Suppressed = false
  Type = 0
FEATURE [Sketcher::SketchObject] Sketch017
  ArcFitTolerance = 1e-06
  AttachmentSupport = -> [Pad010]
  ExternalGeometry = -> [Pad010]
  FullyConstrained = true
  MakeInternals = false
  MapMode = 5
  Placement = pos=(0,-2.261e-13,-678.872) rot=(0,0,1;3.14159rad)
  sketch-geometry (4):
    g0: LineSegment StartX=536.684 StartY=850 StartZ=0 EndX=536.684 EndY=826 EndZ=0
    g1: LineSegment StartX=536.684 StartY=826 StartZ=0 EndX=658.316 EndY=826 EndZ=0
    g2: LineSegment StartX=658.316 StartY=826 StartZ=0 EndX=658.316 EndY=850 EndZ=0
    g3: LineSegment StartX=658.316 StartY=850 StartZ=0 EndX=536.684 EndY=850 EndZ=0
  constraints (12):
    c: Coincident(g0,g1)
    c: Coincident(g1,g2)
    c: Coincident(g2,g3)
    c: Coincident(g3,g0)
    c: Vertical(g0)
    c: Vertical(g2)
    c: Horizontal(g1)
    c: Horizontal(g3)
    c: DistanceY(g2,g-4) = 15
    c: DistanceX(g1,g-4) = 15
    c: DistanceY(g-4,g1) = 1
    c: DistanceX(g-3,g0) = 15
FEATURE [PartDesign::Pocket] Pocket006
  BaseFeature = -> Pad010
  Direction = (0,0,-1)
  Length = 5
  Length2 = 5
  Placement = pos=(0,0,0) rot=(1,0,0;1.5708rad)
  Profile = -> Sketch017
  ReferenceAxis = -> Sketch017 [N_Axis]
  Refine = true
  Suppressed = false
  Type = 1
FEATURE [PartDesign::Fillet] Fillet008
  Base = -> Pocket006 [Edge4,Edge20,Edge21,Edge22]
  BaseFeature = -> Pocket006
  Placement = pos=(0,0,0) rot=(1,0,0;1.5708rad)
  Radius = 15
  Refine = true
  SupportTransform = false
  Suppressed = false
  UseAllEdges = false
FEATURE [PartDesign::Fillet] Fillet009
  Base = -> Fillet008 [Edge8,Edge10,Edge26,Edge20]
  BaseFeature = -> Fillet008
  Placement = pos=(0,0,0) rot=(1,0,0;1.5708rad)
  Radius = 5
  Refine = true
  SupportTransform = false
  Suppressed = false
  UseAllEdges = false
FEATURE [PartDesign::Body] Body005
  AllowCompound = false
  Group = -> [DatumPlane004,CopyPocket005,Sketch016,Pad010,Sketch017,Pocket006,Fillet008,Fillet009]
  Origin = -> Origin010
  Tip = -> Fillet009
FEATURE [PartDesign::ShapeBinder] CopyPocket006
  Placement = pos=(0,0,0) rot=(1,0,0;1.5708rad)
  TraceSupport = false
FEATURE [PartDesign::Plane] DatumPlane005
  AttachmentSupport = -> [CopyPocket006]
  Length = 857.323
  MapMode = 5
  Placement = pos=(0,-825,3.729e-13) rot=(1,0,0;1.5708rad)
  ResizeMode = 0
  Width = 1064.15
FEATURE [Sketcher::SketchObject] Sketch018
  ArcFitTolerance = 1e-06
  AttachmentSupport = -> [CopyPocket006]
  ExternalGeometry = -> [CopyPocket006]
  FullyConstrained = true
  MakeInternals = false
  MapMode = 5
  Placement = pos=(0,-825,3.729e-13) rot=(1,0,0;1.5708rad)
  sketch-geometry (4):
    g0: LineSegment StartX=-673.316 StartY=-858.872 StartZ=0 EndX=-673.316 EndY=-880.143 EndZ=0
    g1: LineSegment StartX=-673.316 StartY=-880.143 StartZ=0 EndX=-521.684 EndY=-880.143 EndZ=0
    g2: LineSegment StartX=-521.684 StartY=-880.143 StartZ=0 EndX=-521.684 EndY=-858.872 EndZ=0
    g3: LineSegment StartX=-521.684 StartY=-858.872 StartZ=0 EndX=-673.316 EndY=-858.872 EndZ=0
  constraints (10):
    c: Coincident(g0,g1)
    c: Coincident(g1,g2)
    c: Coincident(g2,g3)
    c: Coincident(g3,g0)
    c: Vertical(g0)
    c: Vertical(g2)
    c: Horizontal(g1)
    c: Horizontal(g3)
    c: Coincident(g0,g-3)
    c: Coincident(g1,g-4)
FEATURE [PartDesign::Pad] Pad011
  Direction = (0,-1,2e-16)
  Length = 40
  Length2 = 10
  Placement = pos=(0,0,0) rot=(1,0,0;1.5708rad)
  Profile = -> Sketch018
  ReferenceAxis = -> Sketch018 [N_Axis]
  Refine = true
  Suppressed = false
  Type = 0
FEATURE [Sketcher::SketchObject] Sketch019
  ArcFitTolerance = 1e-06
  AttachmentSupport = -> [Pad011]
  ExternalGeometry = -> [Pad011]
  FullyConstrained = true
  MakeInternals = false
  MapMode = 5
  Placement = pos=(0,-2.861e-13,-858.872) rot=(0,0,1;3.14159rad)
  sketch-geometry (4):
    g0: LineSegment StartX=536.684 StartY=850 StartZ=0 EndX=536.684 EndY=826 EndZ=0
    g1: LineSegment StartX=536.684 StartY=826 StartZ=0 EndX=658.316 EndY=826 EndZ=0
    g2: LineSegment StartX=658.316 StartY=826 StartZ=0 EndX=658.316 EndY=850 EndZ=0
    g3: LineSegment StartX=658.316 StartY=850 StartZ=0 EndX=536.684 EndY=850 EndZ=0
  constraints (12):
    c: Coincident(g0,g1)
    c: Coincident(g1,g2)
    c: Coincident(g2,g3)
    c: Coincident(g3,g0)
    c: Vertical(g0)
    c: Vertical(g2)
    c: Horizontal(g1)
    c: Horizontal(g3)
    c: DistanceX(g1,g-4) = 15
    c: DistanceY(g2,g-4) = 15
    c: DistanceX(g-3,g0) = 15
    c: DistanceY(g-4,g1) = 1
FEATURE [PartDesign::Pocket] Pocket007
  BaseFeature = -> Pad011
  Direction = (0,0,-1)
  Length = 1
  Length2 = 5
  Placement = pos=(0,0,0) rot=(1,0,0;1.5708rad)
  Profile = -> Sketch019
  ReferenceAxis = -> Sketch019 [N_Axis]
  Refine = true
  Suppressed = false
  Type = 1
FEATURE [PartDesign::Fillet] Fillet010
  Base = -> Pocket007 [Edge4,Edge20,Edge22,Edge21]
  BaseFeature = -> Pocket007
  Placement = pos=(0,0,0) rot=(1,0,0;1.5708rad)
  Radius = 15
  Refine = true
  SupportTransform = false
  Suppressed = false
  UseAllEdges = false
FEATURE [PartDesign::Fillet] Fillet011
  Base = -> Fillet010 [Edge10,Edge26,Edge8,Edge20]
  BaseFeature = -> Fillet010
  Placement = pos=(0,0,0) rot=(1,0,0;1.5708rad)
  Radius = 5
  Refine = true
  SupportTransform = false
  Suppressed = false
  UseAllEdges = false
FEATURE [PartDesign::Body] Body006
  AllowCompound = false
  Group = -> [DatumPlane005,CopyPocket006,Sketch018,Pad011,Sketch019,Pocket007,Fillet010,Fillet011]
  Origin = -> Origin011
  Tip = -> Fillet011
FEATURE [PartDesign::ShapeBinder] CopyPocket007
  Placement = pos=(0,0,0) rot=(1,0,0;1.5708rad)
  TraceSupport = false
FEATURE [PartDesign::Plane] DatumPlane006
  AttachmentSupport = -> [CopyPocket007]
  Length = 748.322
  MapMode = 5
  Placement = pos=(0,-825,3.729e-13) rot=(1,0,0;1.5708rad)
  ResizeMode = 0
  Width = 171.593
FEATURE [Sketcher::SketchObject] Sketch020
  ArcFitTolerance = 1e-06
  AttachmentSupport = -> [CopyPocket007]
  ExternalGeometry = -> [CopyPocket007]
  FullyConstrained = true
  MakeInternals = false
  MapMode = 5
  Placement = pos=(0,-825,3.729e-13) rot=(1,0,0;1.5708rad)
  sketch-geometry (4):
    g0: LineSegment StartX=515.24 StartY=-68.8715 StartZ=0 EndX=515.24 EndY=-90.1429 EndZ=0
    g1: LineSegment StartX=515.24 StartY=-90.1429 StartZ=0 EndX=666.872 EndY=-90.1429 EndZ=0
    g2: LineSegment StartX=666.872 StartY=-90.1429 StartZ=0 EndX=666.872 EndY=-68.8715 EndZ=0
    g3: LineSegment StartX=666.872 StartY=-68.8715 StartZ=0 EndX=515.24 EndY=-68.8715 EndZ=0
  constraints (10):
    c: Coincident(g0,g1)
    c: Coincident(g1,g2)
    c: Coincident(g2,g3)
    c: Coincident(g3,g0)
    c: Vertical(g0)
    c: Vertical(g2)
    c: Horizontal(g1)
    c: Horizontal(g3)
    c: Coincident(g0,g-3)
    c: Coincident(g1,g-4)
FEATURE [PartDesign::Pad] Pad012
  Direction = (0,-1,2e-16)
  Length = 40
  Length2 = 10
  Placement = pos=(0,0,0) rot=(1,0,0;1.5708rad)
  Profile = -> Sketch020
  ReferenceAxis = -> Sketch020 [N_Axis]
  Refine = true
  Suppressed = false
  Type = 0
FEATURE [Sketcher::SketchObject] Sketch021
  ArcFitTolerance = 1e-06
  AttachmentSupport = -> [Pad012]
  ExternalGeometry = -> [Pad012]
  FullyConstrained = true
  MakeInternals = false
  MapMode = 5
  Placement = pos=(0,-2.29e-14,-68.8715) rot=(0,0,1;3.14159rad)
  sketch-geometry (4):
    g0: LineSegment StartX=-651.872 StartY=850 StartZ=0 EndX=-651.872 EndY=826 EndZ=0
    g1: LineSegment StartX=-651.872 StartY=826 StartZ=0 EndX=-530.24 EndY=826 EndZ=0
    g2: LineSegment StartX=-530.24 StartY=826 StartZ=0 EndX=-530.24 EndY=850 EndZ=0
    g3: LineSegment StartX=-530.24 StartY=850 StartZ=0 EndX=-651.872 EndY=850 EndZ=0
  constraints (12):
    c: Coincident(g0,g1)
    c: Coincident(g1,g2)
    c: Coincident(g2,g3)
    c: Coincident(g3,g0)
    c: Vertical(g0)
    c: Vertical(g2)
    c: Horizontal(g1)
    c: Horizontal(g3)
    c: DistanceX(g2,g-4) = 15
    c: DistanceX(g-3,g0) = 15
    c: DistanceY(g-3,g0) = 1
    c: DistanceY(g2,g-4) = 15
FEATURE [PartDesign::Pocket] Pocket008
  BaseFeature = -> Pad012
  Direction = (0,0,-1)
  Length = 5
  Length2 = 5
  Placement = pos=(0,0,0) rot=(1,0,0;1.5708rad)
  Profile = -> Sketch021
  ReferenceAxis = -> Sketch021 [N_Axis]
  Refine = true
  Suppressed = false
  Type = 1
FEATURE [PartDesign::Fillet] Fillet012
  Base = -> Pocket008 [Edge4,Edge20,Edge21,Edge22]
  BaseFeature = -> Pocket008
  Placement = pos=(0,0,0) rot=(1,0,0;1.5708rad)
  Radius = 15
  Refine = true
  SupportTransform = false
  Suppressed = false
  UseAllEdges = false
FEATURE [PartDesign::Fillet] Fillet013
  Base = -> Fillet012 [Edge10,Edge26,Edge8,Edge20]
  BaseFeature = -> Fillet012
  Placement = pos=(0,0,0) rot=(1,0,0;1.5708rad)
  Radius = 5
  Refine = true
  SupportTransform = false
  Suppressed = false
  UseAllEdges = false
FEATURE [PartDesign::Body] Body007
  AllowCompound = false
  Group = -> [DatumPlane006,CopyPocket007,Sketch020,Pad012,Sketch021,Pocket008,Fillet012,Fillet013]
  Origin = -> Origin012
  Tip = -> Fillet013
FEATURE [PartDesign::ShapeBinder] CopyPocket008
  Placement = pos=(0,0,0) rot=(1,0,0;1.5708rad)
  TraceSupport = false
FEATURE [PartDesign::Plane] DatumPlane007
  AttachmentSupport = -> [CopyPocket008]
  Length = 791.707
  MapMode = 5
  Placement = pos=(0,-825,3.729e-13) rot=(1,0,0;1.5708rad)
  ResizeMode = 0
  Width = 459.977
FEATURE [Sketcher::SketchObject] Sketch022
  ArcFitTolerance = 1e-06
  AttachmentSupport = -> [CopyPocket008]
  ExternalGeometry = -> [CopyPocket008]
  FullyConstrained = true
  MakeInternals = false
  MapMode = 5
  Placement = pos=(0,-825,3.729e-13) rot=(1,0,0;1.5708rad)
  sketch-geometry (4):
    g0: LineSegment StartX=515.24 StartY=-313.872 StartZ=0 EndX=515.24 EndY=-335.143 EndZ=0
    g1: LineSegment StartX=515.24 StartY=-335.143 StartZ=0 EndX=666.872 EndY=-335.143 EndZ=0
    g2: LineSegment StartX=666.872 StartY=-335.143 StartZ=0 EndX=666.872 EndY=-313.872 EndZ=0
    g3: LineSegment StartX=666.872 StartY=-313.872 StartZ=0 EndX=515.24 EndY=-313.872 EndZ=0
  constraints (10):
    c: Coincident(g0,g1)
    c: Coincident(g1,g2)
    c: Coincident(g2,g3)
    c: Coincident(g3,g0)
    c: Vertical(g0)
    c: Vertical(g2)
    c: Horizontal(g1)
    c: Horizontal(g3)
    c: Coincident(g0,g-3)
    c: Coincident(g1,g-4)
FEATURE [PartDesign::Pad] Pad013
  Direction = (0,-1,2e-16)
  Length = 40
  Length2 = 10
  Placement = pos=(0,0,0) rot=(1,0,0;1.5708rad)
  Profile = -> Sketch022
  ReferenceAxis = -> Sketch022 [N_Axis]
  Refine = true
  Suppressed = false
  Type = 0
FEATURE [Sketcher::SketchObject] Sketch023
  ArcFitTolerance = 1e-06
  AttachmentSupport = -> [Pad013]
  ExternalGeometry = -> [Pad013]
  FullyConstrained = true
  MakeInternals = false
  MapMode = 5
  Placement = pos=(0,-1.045e-13,-313.872) rot=(0,0,1;3.14159rad)
  sketch-geometry (4):
    g0: LineSegment StartX=-651.872 StartY=850 StartZ=0 EndX=-651.872 EndY=826 EndZ=0
    g1: LineSegment StartX=-651.872 StartY=826 StartZ=0 EndX=-530.24 EndY=826 EndZ=0
    g2: LineSegment StartX=-530.24 StartY=826 StartZ=0 EndX=-530.24 EndY=850 EndZ=0
    g3: LineSegment StartX=-530.24 StartY=850 StartZ=0 EndX=-651.872 EndY=850 EndZ=0
  constraints (12):
    c: Coincident(g0,g1)
    c: Coincident(g1,g2)
    c: Coincident(g2,g3)
    c: Coincident(g3,g0)
    c: Vertical(g0)
    c: Vertical(g2)
    c: Horizontal(g1)
    c: Horizontal(g3)
    c: DistanceX(g2,g-4) = 15
    c: DistanceY(g2,g-4) = 15
    c: DistanceY(g-4,g1) = 1
    c: DistanceX(g-3,g0) = 15
FEATURE [PartDesign::Pocket] Pocket009
  BaseFeature = -> Pad013
  Direction = (0,0,-1)
  Length = 5
  Length2 = 5
  Placement = pos=(0,0,0) rot=(1,0,0;1.5708rad)
  Profile = -> Sketch023
  ReferenceAxis = -> Sketch023 [N_Axis]
  Refine = true
  Suppressed = false
  Type = 1
FEATURE [PartDesign::Fillet] Fillet014
  Base = -> Pocket009 [Edge4,Edge20,Edge21,Edge22]
  BaseFeature = -> Pocket009
  Placement = pos=(0,0,0) rot=(1,0,0;1.5708rad)
  Radius = 15
  Refine = true
  SupportTransform = false
  Suppressed = false
  UseAllEdges = false
FEATURE [PartDesign::Fillet] Fillet015
  Base = -> Fillet014 [Edge10,Edge26,Edge8,Edge20]
  BaseFeature = -> Fillet014
  Placement = pos=(0,0,0) rot=(1,0,0;1.5708rad)
  Radius = 5
  Refine = true
  SupportTransform = false
  Suppressed = false
  UseAllEdges = false
FEATURE [PartDesign::Body] Body008
  AllowCompound = false
  Group = -> [DatumPlane007,CopyPocket008,Sketch022,Pad013,Sketch023,Pocket009,Fillet014,Fillet015]
  Origin = -> Origin013
  Tip = -> Fillet015
FEATURE [PartDesign::ShapeBinder] CopyPocket009
  Placement = pos=(0,0,0) rot=(1,0,0;1.5708rad)
  TraceSupport = false
FEATURE [PartDesign::Plane] DatumPlane008
  AttachmentSupport = -> [CopyPocket009]
  Length = 814.7
  MapMode = 5
  Placement = pos=(0,-825,3.729e-13) rot=(1,0,0;1.5708rad)
  ResizeMode = 0
  Width = 667.971
FEATURE [Sketcher::SketchObject] Sketch024
  ArcFitTolerance = 1e-06
  AttachmentSupport = -> [CopyPocket009]
  ExternalGeometry = -> [CopyPocket009]
  FullyConstrained = true
  MakeInternals = false
  MapMode = 5
  Placement = pos=(0,-825,3.729e-13) rot=(1,0,0;1.5708rad)
  sketch-geometry (4):
    g0: LineSegment StartX=515.24 StartY=-498.872 StartZ=0 EndX=515.24 EndY=-520.143 EndZ=0
    g1: LineSegment StartX=515.24 StartY=-520.143 StartZ=0 EndX=666.872 EndY=-520.143 EndZ=0
    g2: LineSegment StartX=666.872 StartY=-520.143 StartZ=0 EndX=666.872 EndY=-498.872 EndZ=0
    g3: LineSegment StartX=666.872 StartY=-498.872 StartZ=0 EndX=515.24 EndY=-498.872 EndZ=0
  constraints (10):
    c: Coincident(g0,g1)
    c: Coincident(g1,g2)
    c: Coincident(g2,g3)
    c: Coincident(g3,g0)
    c: Vertical(g0)
    c: Vertical(g2)
    c: Horizontal(g1)
    c: Horizontal(g3)
    c: Coincident(g0,g-3)
    c: Coincident(g1,g-4)
FEATURE [PartDesign::Pad] Pad014
  Direction = (0,-1,2e-16)
  Length = 40
  Length2 = 10
  Placement = pos=(0,0,0) rot=(1,0,0;1.5708rad)
  Profile = -> Sketch024
  ReferenceAxis = -> Sketch024 [N_Axis]
  Refine = true
  Suppressed = false
  Type = 0
FEATURE [Sketcher::SketchObject] Sketch025
  ArcFitTolerance = 1e-06
  AttachmentSupport = -> [Pad014]
  ExternalGeometry = -> [Pad014]
  FullyConstrained = true
  MakeInternals = false
  MapMode = 5
  Placement = pos=(0,-1.662e-13,-498.872) rot=(0,0,1;3.14159rad)
  sketch-geometry (4):
    g0: LineSegment StartX=-651.872 StartY=850 StartZ=0 EndX=-651.872 EndY=826 EndZ=0
    g1: LineSegment StartX=-651.872 StartY=826 StartZ=0 EndX=-530.24 EndY=826 EndZ=0
    g2: LineSegment StartX=-530.24 StartY=826 StartZ=0 EndX=-530.24 EndY=850 EndZ=0
    g3: LineSegment StartX=-530.24 StartY=850 StartZ=0 EndX=-651.872 EndY=850 EndZ=0
  constraints (12):
    c: Coincident(g0,g1)
    c: Coincident(g1,g2)
    c: Coincident(g2,g3)
    c: Coincident(g3,g0)
    c: Vertical(g0)
    c: Vertical(g2)
    c: Horizontal(g1)
    c: Horizontal(g3)
    c: DistanceX(g2,g-4) = 15
    c: DistanceY(g2,g-4) = 15
    c: DistanceY(g-4,g1) = 1
    c: DistanceX(g-3,g0) = 15
FEATURE [PartDesign::Pocket] Pocket010
  BaseFeature = -> Pad014
  Direction = (0,0,-1)
  Length = 5
  Length2 = 5
  Placement = pos=(0,0,0) rot=(1,0,0;1.5708rad)
  Profile = -> Sketch025
  ReferenceAxis = -> Sketch025 [N_Axis]
  Refine = true
  Suppressed = false
  Type = 1
FEATURE [PartDesign::Fillet] Fillet016
  Base = -> Pocket010 [Edge20,Edge4,Edge22,Edge21]
  BaseFeature = -> Pocket010
  Placement = pos=(0,0,0) rot=(1,0,0;1.5708rad)
  Radius = 15
  Refine = true
  SupportTransform = false
  Suppressed = false
  UseAllEdges = false
FEATURE [PartDesign::Fillet] Fillet017
  Base = -> Fillet016 [Edge10,Edge8,Edge26,Edge20]
  BaseFeature = -> Fillet016
  Placement = pos=(0,0,0) rot=(1,0,0;1.5708rad)
  Radius = 5
  Refine = true
  SupportTransform = false
  Suppressed = false
  UseAllEdges = false
FEATURE [PartDesign::Body] Body009
  AllowCompound = false
  Group = -> [DatumPlane008,CopyPocket009,Sketch024,Pad014,Sketch025,Pocket010,Fillet016,Fillet017]
  Origin = -> Origin014
  Tip = -> Fillet017
FEATURE [PartDesign::ShapeBinder] CopyPocket010
  Placement = pos=(0,0,0) rot=(1,0,0;1.5708rad)
  TraceSupport = false
FEATURE [PartDesign::Plane] DatumPlane009
  AttachmentSupport = -> [CopyPocket010]
  Length = 833.535
  MapMode = 5
  Placement = pos=(0,-825,3.729e-13) rot=(1,0,0;1.5708rad)
  ResizeMode = 0
  Width = 866.806
FEATURE [Sketcher::SketchObject] Sketch026
  ArcFitTolerance = 1e-06
  AttachmentSupport = -> [CopyPocket010]
  ExternalGeometry = -> [CopyPocket010]
  FullyConstrained = true
  MakeInternals = false
  MapMode = 5
  Placement = pos=(0,-825,3.729e-13) rot=(1,0,0;1.5708rad)
  sketch-geometry (4):
    g0: LineSegment StartX=515.24 StartY=-678.872 StartZ=0 EndX=515.24 EndY=-700.143 EndZ=0
    g1: LineSegment StartX=515.24 StartY=-700.143 StartZ=0 EndX=666.872 EndY=-700.143 EndZ=0
    g2: LineSegment StartX=666.872 StartY=-700.143 StartZ=0 EndX=666.872 EndY=-678.872 EndZ=0
    g3: LineSegment StartX=666.872 StartY=-678.872 StartZ=0 EndX=515.24 EndY=-678.872 EndZ=0
  constraints (10):
    c: Coincident(g0,g1)
    c: Coincident(g1,g2)
    c: Coincident(g2,g3)
    c: Coincident(g3,g0)
    c: Vertical(g0)
    c: Vertical(g2)
    c: Horizontal(g1)
    c: Horizontal(g3)
    c: Coincident(g0,g-3)
    c: Coincident(g1,g-4)
FEATURE [PartDesign::Pad] Pad015
  Direction = (0,-1,2e-16)
  Length = 40
  Length2 = 10
  Placement = pos=(0,0,0) rot=(1,0,0;1.5708rad)
  Profile = -> Sketch026
  ReferenceAxis = -> Sketch026 [N_Axis]
  Refine = true
  Suppressed = false
  Type = 0
FEATURE [Sketcher::SketchObject] Sketch027
  ArcFitTolerance = 1e-06
  AttachmentSupport = -> [Pad015]
  ExternalGeometry = -> [Pad015]
  FullyConstrained = true
  MakeInternals = false
  MapMode = 5
  Placement = pos=(0,-2.261e-13,-678.872) rot=(0,0,1;3.14159rad)
  sketch-geometry (4):
    g0: LineSegment StartX=-651.872 StartY=850 StartZ=0 EndX=-651.872 EndY=826 EndZ=0
    g1: LineSegment StartX=-651.872 StartY=826 StartZ=0 EndX=-530.24 EndY=826 EndZ=0
    g2: LineSegment StartX=-530.24 StartY=826 StartZ=0 EndX=-530.24 EndY=850 EndZ=0
    g3: LineSegment StartX=-530.24 StartY=850 StartZ=0 EndX=-651.872 EndY=850 EndZ=0
  constraints (12):
    c: Coincident(g0,g1)
    c: Coincident(g1,g2)
    c: Coincident(g2,g3)
    c: Coincident(g3,g0)
    c: Vertical(g0)
    c: Vertical(g2)
    c: Horizontal(g1)
    c: Horizontal(g3)
    c: DistanceX(g-3,g0) = 15
    c: DistanceY(g2,g-4) = 15
    c: DistanceX(g2,g-4) = 15
    c: DistanceY(g-4,g1) = 1
FEATURE [PartDesign::Pocket] Pocket011
  BaseFeature = -> Pad015
  Direction = (0,0,-1)
  Length = 5
  Length2 = 5
  Placement = pos=(0,0,0) rot=(1,0,0;1.5708rad)
  Profile = -> Sketch027
  ReferenceAxis = -> Sketch027 [N_Axis]
  Refine = true
  Suppressed = false
  Type = 1
FEATURE [PartDesign::Fillet] Fillet018
  Base = -> Pocket011 [Edge4,Edge20,Edge21,Edge22]
  BaseFeature = -> Pocket011
  Placement = pos=(0,0,0) rot=(1,0,0;1.5708rad)
  Radius = 15
  Refine = true
  SupportTransform = false
  Suppressed = false
  UseAllEdges = false
FEATURE [PartDesign::Fillet] Fillet019
  Base = -> Fillet018 [Edge10,Edge26,Edge8,Edge20]
  BaseFeature = -> Fillet018
  Placement = pos=(0,0,0) rot=(1,0,0;1.5708rad)
  Radius = 5
  Refine = true
  SupportTransform = false
  Suppressed = false
  UseAllEdges = false
FEATURE [PartDesign::Body] Body010
  AllowCompound = false
  Group = -> [DatumPlane009,CopyPocket010,Sketch026,Pad015,Sketch027,Pocket011,Fillet018,Fillet019]
  Origin = -> Origin015
  Tip = -> Fillet019
FEATURE [PartDesign::ShapeBinder] CopyPocket011
  Placement = pos=(0,0,0) rot=(1,0,0;1.5708rad)
  TraceSupport = false
FEATURE [PartDesign::Plane] DatumPlane010
  AttachmentSupport = -> [CopyPocket011]
  Length = 850.143
  MapMode = 5
  Placement = pos=(0,-825,3.729e-13) rot=(1,0,0;1.5708rad)
  ResizeMode = 0
  Width = 1063.41
FEATURE [Sketcher::SketchObject] Sketch028
  ArcFitTolerance = 1e-06
  AttachmentSupport = -> [CopyPocket011]
  ExternalGeometry = -> [CopyPocket011]
  FullyConstrained = true
  MakeInternals = false
  MapMode = 5
  Placement = pos=(0,-825,3.729e-13) rot=(1,0,0;1.5708rad)
  sketch-geometry (4):
    g0: LineSegment StartX=515.24 StartY=-858.872 StartZ=0 EndX=515.24 EndY=-880.143 EndZ=0
    g1: LineSegment StartX=515.24 StartY=-880.143 StartZ=0 EndX=666.872 EndY=-880.143 EndZ=0
    g2: LineSegment StartX=666.872 StartY=-880.143 StartZ=0 EndX=666.872 EndY=-858.872 EndZ=0
    g3: LineSegment StartX=666.872 StartY=-858.872 StartZ=0 EndX=515.24 EndY=-858.872 EndZ=0
  constraints (10):
    c: Coincident(g0,g1)
    c: Coincident(g1,g2)
    c: Coincident(g2,g3)
    c: Coincident(g3,g0)
    c: Vertical(g0)
    c: Vertical(g2)
    c: Horizontal(g1)
    c: Horizontal(g3)
    c: Coincident(g0,g-3)
    c: Coincident(g1,g-4)
FEATURE [PartDesign::Pad] Pad016
  Direction = (0,-1,2e-16)
  Length = 40
  Length2 = 10
  Placement = pos=(0,0,0) rot=(1,0,0;1.5708rad)
  Profile = -> Sketch028
  ReferenceAxis = -> Sketch028 [N_Axis]
  Refine = true
  Suppressed = false
  Type = 0
FEATURE [Sketcher::SketchObject] Sketch029
  ArcFitTolerance = 1e-06
  AttachmentSupport = -> [Pad016]
  ExternalGeometry = -> [Pad016]
  FullyConstrained = true
  MakeInternals = false
  MapMode = 5
  Placement = pos=(0,-2.861e-13,-858.872) rot=(0,0,1;3.14159rad)
  sketch-geometry (4):
    g0: LineSegment StartX=-651.872 StartY=850 StartZ=0 EndX=-651.872 EndY=826 EndZ=0
    g1: LineSegment StartX=-651.872 StartY=826 StartZ=0 EndX=-530.24 EndY=826 EndZ=0
    g2: LineSegment StartX=-530.24 StartY=826 StartZ=0 EndX=-530.24 EndY=850 EndZ=0
    g3: LineSegment StartX=-530.24 StartY=850 StartZ=0 EndX=-651.872 EndY=850 EndZ=0
  constraints (12):
    c: Coincident(g0,g1)
    c: Coincident(g1,g2)
    c: Coincident(g2,g3)
    c: Coincident(g3,g0)
    c: Vertical(g0)
    c: Vertical(g2)
    c: Horizontal(g1)
    c: Horizontal(g3)
    c: DistanceY(g-4,g1) = 1
    c: DistanceX(g2,g-4) = 15
    c: DistanceY(g2,g-4) = 15
    c: DistanceX(g-3,g0) = 15
FEATURE [PartDesign::Pocket] Pocket012
  BaseFeature = -> Pad016
  Direction = (0,0,-1)
  Length = 5
  Length2 = 5
  Placement = pos=(0,0,0) rot=(1,0,0;1.5708rad)
  Profile = -> Sketch029
  ReferenceAxis = -> Sketch029 [N_Axis]
  Refine = true
  Suppressed = false
  Type = 1
FEATURE [PartDesign::Fillet] Fillet020
  Base = -> Pocket012 [Edge4,Edge20,Edge22,Edge21]
  BaseFeature = -> Pocket012
  Placement = pos=(0,0,0) rot=(1,0,0;1.5708rad)
  Radius = 15
  Refine = true
  SupportTransform = false
  Suppressed = false
  UseAllEdges = false
FEATURE [PartDesign::Fillet] Fillet021
  Base = -> Fillet020 [Edge8,Edge10,Edge26,Edge20]
  BaseFeature = -> Fillet020
  Placement = pos=(0,0,0) rot=(1,0,0;1.5708rad)
  Radius = 5
  Refine = true
  SupportTransform = false
  Suppressed = false
  UseAllEdges = false
FEATURE [PartDesign::Body] Body011
  AllowCompound = false
  Group = -> [DatumPlane010,CopyPocket011,Sketch028,Pad016,Sketch029,Pocket012,Fillet020,Fillet021]
  Origin = -> Origin016
  Tip = -> Fillet021
PROVENANCE & LICENSES
A FreeCAD (.FCStd) document from a public repository crawl; recipes are the document's own serialized feature recipes (and, for linked parts, companion documents' recipes).
License: as declared in the source repository (recorded in the dataset sidecar).
